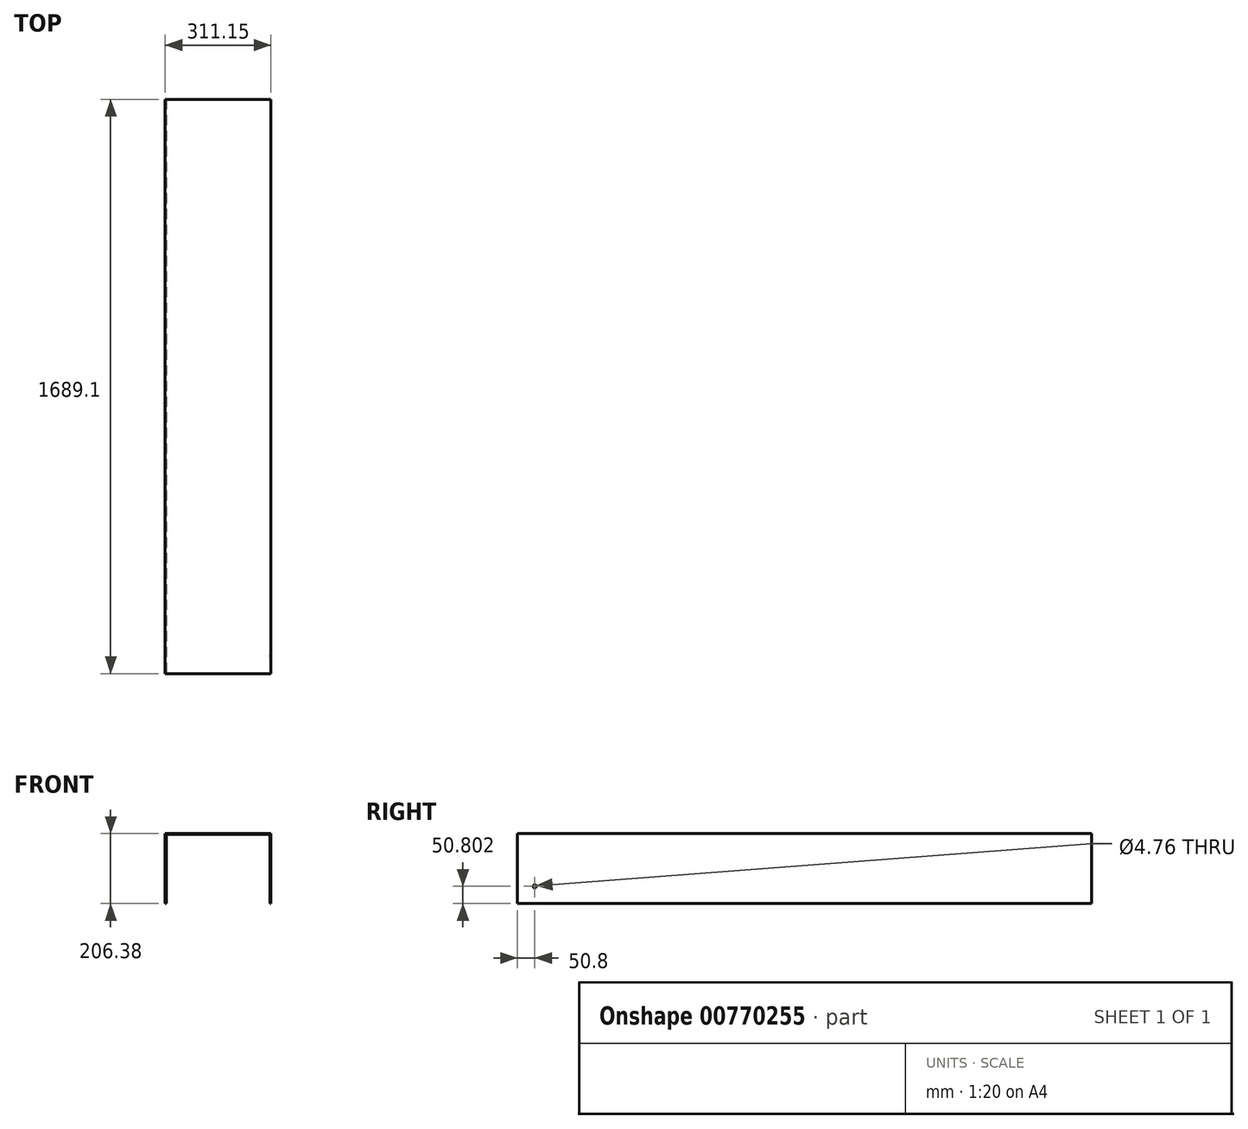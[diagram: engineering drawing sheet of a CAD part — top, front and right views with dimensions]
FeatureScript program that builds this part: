
annotation { "Feature Type Name" : "Feature", "Feature Type Description" : "" }
export const myFeature = defineFeature(function(context is Context, id is Id, definition is map)
    precondition{}
    {
        {
            var Q0;
            Q0=qCreatedBy(makeId("Front.planeOp"),FACE);
            var sketch = newSketch(context, id + "F0", { "sketchPlane" : qUnion([Q0])});
            skLineSegment(sketch, "E0.bottom", {"start": v(155.57, 103.19) * mm, "end": v(-155.58, 103.19) * mm});
            skLineSegment(sketch, "E0.top", {"start": v(155.58, -103.19) * mm, "end": v(152.4, -103.19) * mm});
            skLineSegment(sketch, "E0.left", {"start": v(155.57, 103.19) * mm, "end": v(155.58, -103.19) * mm});
            skLineSegment(sketch, "E0.right", {"start": v(-155.58, 103.19) * mm, "end": v(-155.57, -103.19) * mm});
            skPoint(sketch, "E0.middle", {"position": v(0, 0) * mm});
            skLineSegment(sketch, "E1.0", {"start": v(152.4, 100.01) * mm, "end": v(-152.4, 100.01) * mm});
            skLineSegment(sketch, "E2.0", {"start": v(-152.4, 100.01) * mm, "end": v(-152.4, -103.19) * mm});
            skLineSegment(sketch, "E3.0", {"start": v(152.4, 100.01) * mm, "end": v(152.4, -103.19) * mm});
            skLineSegment(sketch, "E4.trimOffspring", {"start": v(-152.4, -103.19) * mm, "end": v(-155.57, -103.19) * mm});
            skSolve(sketch);
        }
        {
            var Q0;
            Q0=makeQuery(id+"F0.imprint","IMPRINT",FACE,{"disambiguationData":[TD([[makeQuery(id+"F0.imprint","IMPRINT",EDGE,{"derivedFrom":sQuery(id+"F0.wireOp",EDGE,"E0.bottom")}),1.0]])]});
            extrude(context, id + "F1", {"entities" : qUnion([Q0]), "endBound" : BoundingType.SYMMETRIC, "oppositeDirection" : true, "depth" : 1689.1 * mm, "offsetDistance" : 25.4 * mm});
        }
        {
            var Q0;
            Q0=makeQuery(id+"F1.opExtrude","SWEPT_FACE",FACE,{"disambiguationData":[OSD([sQuery(id+"F0.wireOp",EDGE,"E0.left")])]});
            var sketch = newSketch(context, id + "F2", { "sketchPlane" : qUnion([Q0])});
            skPoint(sketch, "E5", {"position": v(-793.75, -52.39) * mm});
            skSolve(sketch);
        }
        {
            var Q0;
            Q0=sQuery(id+"F2.wireOp",VERTEX,"E5");
            var Q1;
            Q1=makeQuery(id+"F1.opExtrude","SWEPT_BODY",BODY,{"disambiguationData":[OSD([sQuery(id+"F0.wireOp",EDGE,"E0.bottom"),sQuery(id+"F0.wireOp",EDGE,"E0.top"),sQuery(id+"F0.wireOp",EDGE,"E0.left"),sQuery(id+"F0.wireOp",EDGE,"E0.right"),sQuery(id+"F0.wireOp",EDGE,"E1.0"),sQuery(id+"F0.wireOp",EDGE,"E2.0"),sQuery(id+"F0.wireOp",EDGE,"E3.0"),sQuery(id+"F0.wireOp",EDGE,"E4.trimOffspring")])]});
            hole(context, id + "F3", {"style" : HoleStyle.C_SINK, "endStyle" : HoleEndStyle.BLIND, "holeDiameter" : 4.76 * mm, "cSinkDiameter" : 9.52 * mm, "cSinkAngle" : 90 * degree, "majorDiameter" : 6.35 * mm, "holeDepth" : 25.4 * mm, "isTappedThrough" : true, "tappedDepth" : 12.7 * mm, "tapClearance" : 3, "locations" : qUnion([Q0]), "scope" : qUnion([Q1])});
        }
    });
